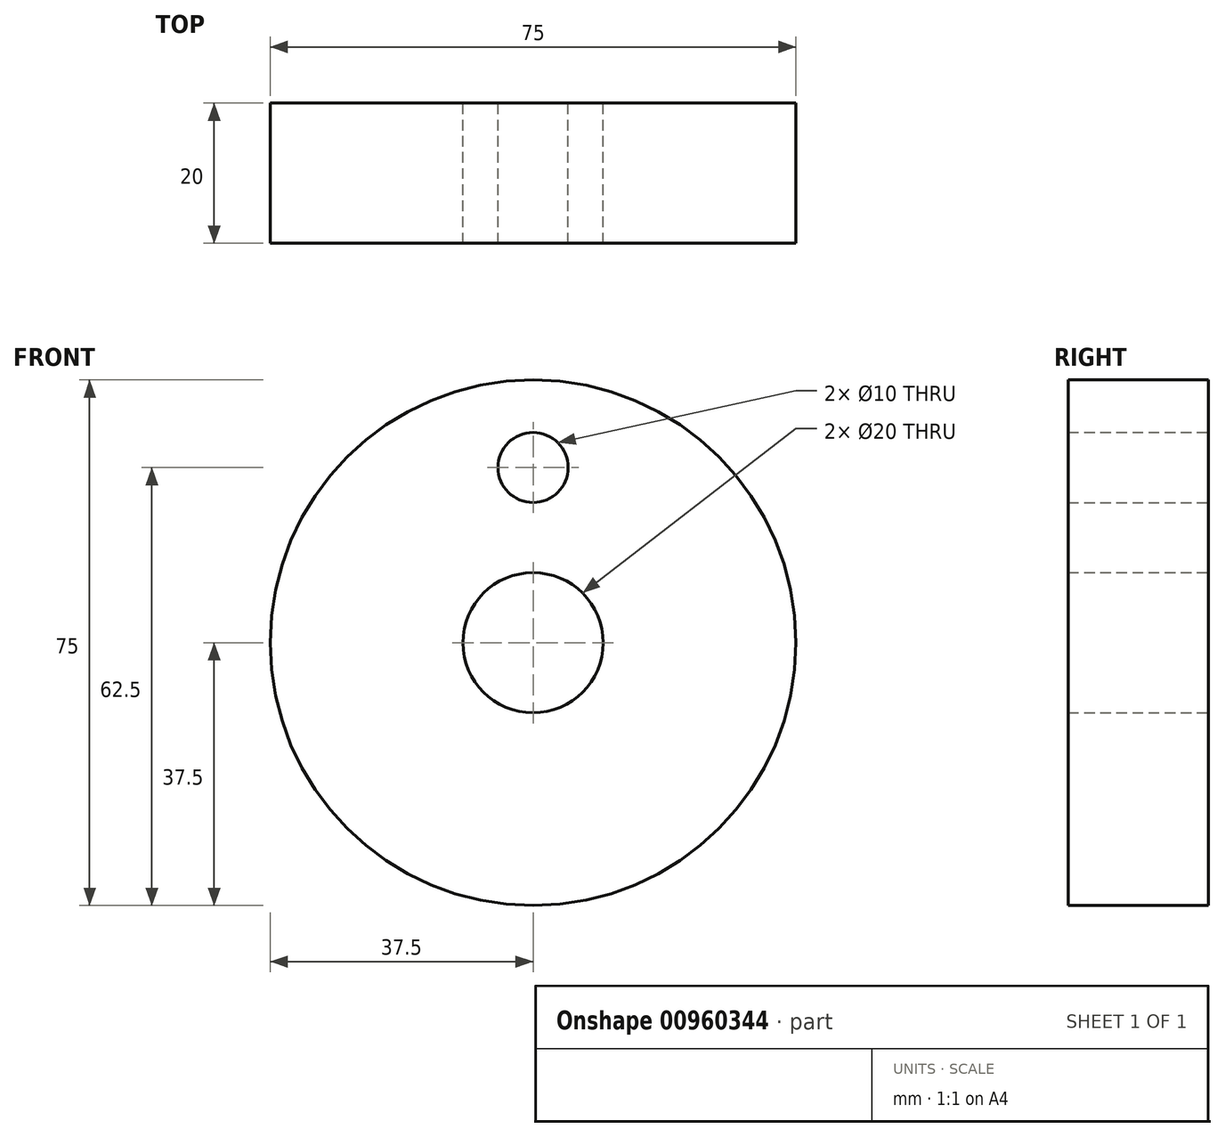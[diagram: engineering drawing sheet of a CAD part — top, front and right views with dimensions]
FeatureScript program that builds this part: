
annotation { "Feature Type Name" : "Feature", "Feature Type Description" : "" }
export const myFeature = defineFeature(function(context is Context, id is Id, definition is map)
    precondition{}
    {
        {
            var Q0;
            Q0=qCreatedBy(makeId("Front.planeOp"),FACE);
            var sketch = newSketch(context, id + "F0", { "sketchPlane" : qUnion([Q0])});
            skCircle(sketch, "E0", {"center": v(0, 0) * mm, "radius": 37.5 * mm});
            skCircle(sketch, "E1", {"center": v(0, 25) * mm, "radius": 5 * mm});
            skLineSegment(sketch, "E2", {"start": v(-71.27, 0) * mm, "end": v(71.27, 0) * mm, "construction": true});
            skLineSegment(sketch, "E3", {"start": v(0, 71.45) * mm, "end": v(0, -71.45) * mm, "construction": true});
            skCircle(sketch, "E4", {"center": v(0, 0) * mm, "radius": 10 * mm});
            skSolve(sketch);
        }
        {
            var Q0;
            Q0=qSketchRegion(id+"F0",true);
            extrude(context, id + "F1", {"entities" : qUnion([Q0]), "depth" : 20 * mm, "offsetDistance" : 25 * mm});
        }
    });
